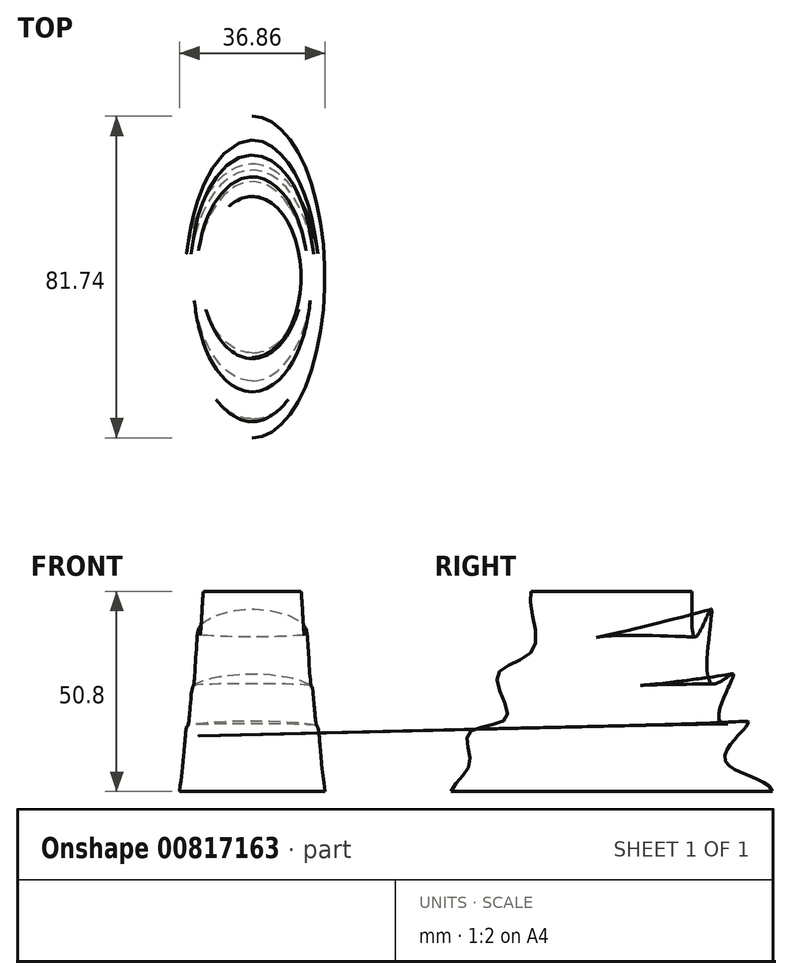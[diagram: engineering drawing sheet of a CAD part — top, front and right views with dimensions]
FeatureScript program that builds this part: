
annotation { "Feature Type Name" : "Feature", "Feature Type Description" : "" }
export const myFeature = defineFeature(function(context is Context, id is Id, definition is map)
    precondition{}
    {
        {
            var Q0;
            Q0=qCreatedBy(makeId("Top.planeOp"),FACE);
            cPlane(context, id + "F0", {"entities" : qUnion([Q0]), "cplaneType" : CPlaneType.OFFSET, "offset" : 50.8 * mm, "width" : 152.4 * mm, "height" : 152.4 * mm});
        }
        {
            var Q0;
            Q0=qCreatedBy(makeId("Top.planeOp"),FACE);
            var sketch = newSketch(context, id + "F1", { "sketchPlane" : qUnion([Q0])});
            skEllipse(sketch, "E0", {"center": v(0, 0) * mm, "majorRadius": 40.87 * mm, "minorRadius": 18.43 * mm, "majorAxis": v(0, 1)});
            skPoint(sketch, "E1", {"position": v(0, 40.87) * mm});
            skPoint(sketch, "E2", {"position": v(0, -40.87) * mm});
            skSolve(sketch);
        }
        {
            var Q0;
            Q0=qCreatedBy(id+"F0.planeOp",FACE);
            var sketch = newSketch(context, id + "F2", { "sketchPlane" : qUnion([Q0])});
            skEllipse(sketch, "E3", {"center": v(0, 0) * mm, "majorRadius": 20.44 * mm, "minorRadius": 12.4 * mm, "majorAxis": v(0, 1)});
            skPoint(sketch, "E4", {"position": v(0, 20.44) * mm});
            skPoint(sketch, "E5", {"position": v(0, -20.44) * mm});
            skSolve(sketch);
        }
        {
            var Q0;
            Q0=qCreatedBy(makeId("Right.planeOp"),FACE);
            var sketch = newSketch(context, id + "F3", { "sketchPlane" : qUnion([Q0])});
            skFitSpline(sketch, "E6", {"points": [v(-20.44, 50.8) * mm, v(-19.84, 36.19) * mm, v(-29.06, 29.47) * mm, v(-26.6, 18.8) * mm, v(-36.12, 14.99) * mm, v(-36.09, 7.14) * mm, v(-40.87, 0) * mm], "startDerivative": vector(-20.87, -50.45) * mm, "endDerivative": vector(-20.87, -50.45) * mm});
            skSolve(sketch);
        }
        {
            var Q0;
            Q0=qCreatedBy(makeId("Right.planeOp"),FACE);
            var sketch = newSketch(context, id + "F4", { "sketchPlane" : qUnion([Q0])});
            skFitSpline(sketch, "E7", {"points": [v(40.87, 0) * mm, v(28.7, 8.28) * mm, v(34.73, 17.66) * mm, v(27.45, 17.88) * mm, v(30.91, 29.84) * mm, v(25.28, 27.47) * mm, v(25.3, 46.3) * mm, v(21.15, 39.19) * mm, v(20.44, 50.8) * mm], "startDerivative": vector(-31.13, 79.1) * mm, "endDerivative": vector(-2.08, 5.14) * mm});
            skSolve(sketch);
        }
        {
            var Q0;
            Q0=makeQuery(id+"F1.imprint","IMPRINT",FACE,{"disambiguationData":[TD([[makeQuery(id+"F1.imprint","IMPRINT",EDGE,{"derivedFrom":sQuery(id+"F1.wireOp",EDGE,"E0")}),1.0]])]});
            var Q1;
            Q1=makeQuery(id+"F2.imprint","IMPRINT",FACE,{"disambiguationData":[TD([[makeQuery(id+"F2.imprint","IMPRINT",EDGE,{"derivedFrom":sQuery(id+"F2.wireOp",EDGE,"E3")}),1.0]])]});
            var Q2;
            Q2=sQuery(id+"F3.wireOp",EDGE,"E6");
            var Q3;
            Q3=sQuery(id+"F4.wireOp",EDGE,"E7");
            loft(context, id + "F5", {"addGuides" : true, "sheetProfilesArray" : [{ "sheetProfileEntities" : qUnion([Q0]) }, { "sheetProfileEntities" : qUnion([Q1]) }], "guidesArray" : [{ "guideEntities" : qUnion([Q2]), "guideDerivativeType" : LoftGuideDerivativeType.DEFAULT, "guideDerivativeMagnitude" : 1 }, { "guideEntities" : qUnion([Q3]), "guideDerivativeType" : LoftGuideDerivativeType.DEFAULT, "guideDerivativeMagnitude" : 1 }]});
        }
    });
